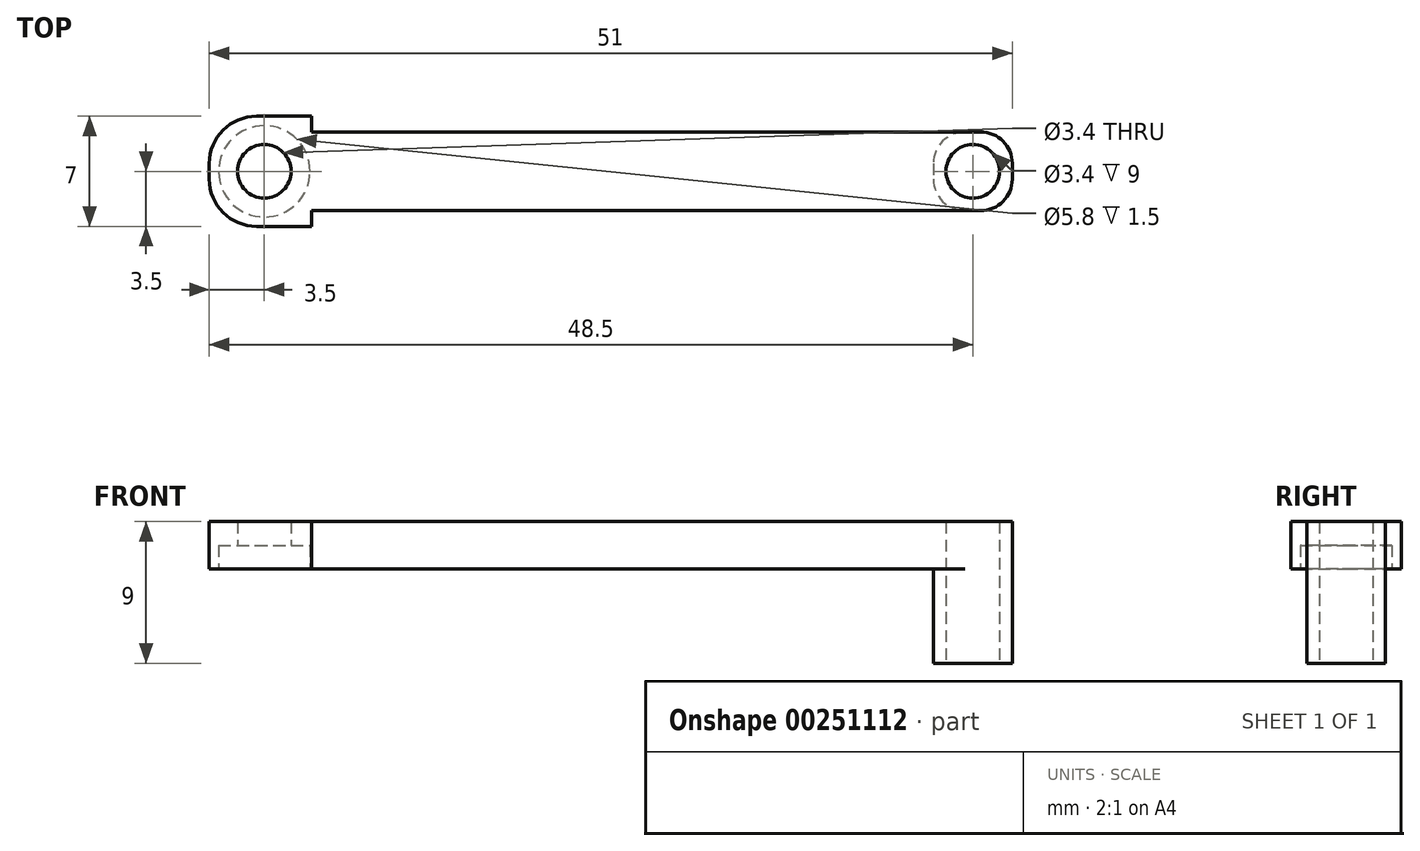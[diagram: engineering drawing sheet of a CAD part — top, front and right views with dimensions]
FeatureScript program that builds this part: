
annotation { "Feature Type Name" : "Feature", "Feature Type Description" : "" }
export const myFeature = defineFeature(function(context is Context, id is Id, definition is map)
    precondition{}
    {
        {
            var Q0;
            Q0=qCreatedBy(makeId("Top.planeOp"),FACE);
            var sketch = newSketch(context, id + "F0", { "sketchPlane" : qUnion([Q0])});
            skCircle(sketch, "E0", {"center": v(0, 0) * mm, "radius": 1.7 * mm});
            skCircle(sketch, "E1", {"center": v(45, 0) * mm, "radius": 1.7 * mm});
            skLineSegment(sketch, "E2", {"start": v(0, 0) * mm, "end": v(45, 0) * mm, "construction": true});
            skLineSegment(sketch, "E3", {"start": v(-2.5, 0) * mm, "end": v(-2.5, 2.5) * mm});
            skLineSegment(sketch, "E4", {"start": v(-2.5, 2.5) * mm, "end": v(47.5, 2.5) * mm});
            skLineSegment(sketch, "E5", {"start": v(47.5, 2.5) * mm, "end": v(47.5, 0) * mm});
            skLineSegment(sketch, "E6.MirrorCS", {"start": v(-2.5, 0) * mm, "end": v(-2.5, -2.5) * mm});
            skLineSegment(sketch, "E7.MirrorCS", {"start": v(-2.5, -2.5) * mm, "end": v(47.5, -2.5) * mm});
            skLineSegment(sketch, "E8.MirrorCS", {"start": v(47.5, -2.5) * mm, "end": v(47.5, 0) * mm});
            skSolve(sketch);
        }
        {
            var Q0;
            Q0=makeQuery(id+"F0.imprint","IMPRINT",FACE,{"disambiguationData":[TD([[makeQuery(id+"F0.imprint","IMPRINT",EDGE,{"derivedFrom":sQuery(id+"F0.wireOp",EDGE,"E0")}),-1.0]])]});
            extrude(context, id + "F1", {"entities" : qUnion([Q0]), "depth" : 3 * mm});
        }
        {
            var Q0;
            Q0=makeQuery(id+"F1.opExtrude","SWEPT_EDGE",EDGE,{"disambiguationData":[OSD([sQuery(id+"F0.wireOp",EDGE,"E3"),sQuery(id+"F0.wireOp",EDGE,"E4")])]});
            var Q1;
            Q1=makeQuery(id+"F1.opExtrude","SWEPT_EDGE",EDGE,{"disambiguationData":[OSD([sQuery(id+"F0.wireOp",EDGE,"E6.MirrorCS"),sQuery(id+"F0.wireOp",EDGE,"E7.MirrorCS")])]});
            var Q2;
            Q2=makeQuery(id+"F1.opExtrude","SWEPT_EDGE",EDGE,{"disambiguationData":[OSD([sQuery(id+"F0.wireOp",EDGE,"E4"),sQuery(id+"F0.wireOp",EDGE,"E5")])]});
            var Q3;
            Q3=makeQuery(id+"F1.opExtrude","SWEPT_EDGE",EDGE,{"disambiguationData":[OSD([sQuery(id+"F0.wireOp",EDGE,"E7.MirrorCS"),sQuery(id+"F0.wireOp",EDGE,"E8.MirrorCS")])]});
            fillet(context, id + "F2", {"entities" : qUnion([Q0, Q1, Q2, Q3]), "radius" : 2 * mm, "tangentPropagation" : true, "allowEdgeOverflow" : false});
        }
        {
            var Q0;
            Q0=makeQuery(id+"F1.opExtrude","CAP_FACE",FACE,{"disambiguationData":[OSD([sQuery(id+"F0.wireOp",EDGE,"E0"),sQuery(id+"F0.wireOp",EDGE,"E1"),sQuery(id+"F0.wireOp",EDGE,"E3"),sQuery(id+"F0.wireOp",EDGE,"E4"),sQuery(id+"F0.wireOp",EDGE,"E5"),sQuery(id+"F0.wireOp",EDGE,"E6.MirrorCS"),sQuery(id+"F0.wireOp",EDGE,"E7.MirrorCS"),sQuery(id+"F0.wireOp",EDGE,"E8.MirrorCS")])],"isStart":true});
            var sketch = newSketch(context, id + "F3", { "sketchPlane" : qUnion([Q0])});
            skArc(sketch, "E9.0", {"start": v(45.5, -2.5) * mm, "mid": v(46.91, -1.91) * mm, "end": v(47.5, -0.5) * mm});
            skPoint(sketch, "E10.0", {"position": v(47.5, 0) * mm});
            skPoint(sketch, "E11.0", {"position": v(46.91, 1.91) * mm});
            skArc(sketch, "E12.0", {"start": v(47.5, 0.5) * mm, "mid": v(46.91, 1.91) * mm, "end": v(45.5, 2.5) * mm});
            skLineSegment(sketch, "E13", {"start": v(45.5, -2.5) * mm, "end": v(42.5, -2.5) * mm});
            skLineSegment(sketch, "E14", {"start": v(42.5, -2.5) * mm, "end": v(42.5, 2.5) * mm});
            skLineSegment(sketch, "E15", {"start": v(42.5, 2.5) * mm, "end": v(45.5, 2.5) * mm});
            skCircle(sketch, "E16.0", {"center": v(45, 0) * mm, "radius": 1.7 * mm});
            skSolve(sketch);
        }
        {
            var Q0;
            Q0=makeQuery(id+"F3.imprint","IMPRINT",FACE,{"disambiguationData":[TD([[makeQuery(id+"F3.imprint","IMPRINT",EDGE,{"derivedFrom":sQuery(id+"F3.wireOp",EDGE,"E9.0")}),1.0]])]});
            extrude(context, id + "F4", {"entities" : qUnion([Q0]), "operationType" : NewBodyOperationType.ADD, "depth" : 6 * mm});
        }
        {
            var Q0;
            Q0=makeQuery(id+"F4.opExtrude","SWEPT_EDGE",EDGE,{"disambiguationData":[OSD([sQuery(id+"F0.wireOp",EDGE,"E4"),sQuery(id+"F3.wireOp",EDGE,"E13"),sQuery(id+"F3.wireOp",EDGE,"E14")])]});
            var Q1;
            Q1=makeQuery(id+"F4.opExtrude","SWEPT_EDGE",EDGE,{"disambiguationData":[OSD([sQuery(id+"F0.wireOp",EDGE,"E7.MirrorCS"),sQuery(id+"F3.wireOp",EDGE,"E14"),sQuery(id+"F3.wireOp",EDGE,"E15")])]});
            fillet(context, id + "F5", {"entities" : qUnion([Q0, Q1]), "radius" : 2 * mm, "tangentPropagation" : true, "allowEdgeOverflow" : false});
        }
        {
            var Q0;
            Q0=makeQuery(id+"F1.opExtrude","CAP_FACE",FACE,{"disambiguationData":[OSD([sQuery(id+"F0.wireOp",EDGE,"E0"),sQuery(id+"F0.wireOp",EDGE,"E1"),sQuery(id+"F0.wireOp",EDGE,"E3"),sQuery(id+"F0.wireOp",EDGE,"E4"),sQuery(id+"F0.wireOp",EDGE,"E5"),sQuery(id+"F0.wireOp",EDGE,"E6.MirrorCS"),sQuery(id+"F0.wireOp",EDGE,"E7.MirrorCS"),sQuery(id+"F0.wireOp",EDGE,"E8.MirrorCS")])],"isStart":false});
            var sketch = newSketch(context, id + "F6", { "sketchPlane" : qUnion([Q0])});
            skCircle(sketch, "E17.0", {"center": v(0, 0) * mm, "radius": 1.7 * mm});
            skArc(sketch, "E17.1", {"start": v(-0.5, 2.5) * mm, "mid": v(-1.91, 1.91) * mm, "end": v(-2.5, 0.5) * mm});
            skArc(sketch, "E17.2", {"start": v(-2.5, -0.5) * mm, "mid": v(-1.91, -1.91) * mm, "end": v(-0.5, -2.5) * mm});
            skCircle(sketch, "E17.4", {"center": v(0, 0) * mm, "radius": 1.7 * mm});
            skArc(sketch, "E17.5", {"start": v(-2.5, 0.5) * mm, "mid": v(-1.91, 1.91) * mm, "end": v(-0.5, 2.5) * mm});
            skArc(sketch, "E17.6", {"start": v(-0.5, -2.5) * mm, "mid": v(-1.91, -1.91) * mm, "end": v(-2.5, -0.5) * mm});
            skLineSegment(sketch, "E17.8", {"start": v(-2.5, -0.5) * mm, "end": v(-2.5, 0.5) * mm});
            skLineSegment(sketch, "E17.11", {"start": v(-2.5, -0.5) * mm, "end": v(-2.5, 0.5) * mm});
            skArc(sketch, "E18.0", {"start": v(-3.5, 0.5) * mm, "mid": v(-2.62, 2.62) * mm, "end": v(-0.5, 3.5) * mm});
            skLineSegment(sketch, "E18.1", {"start": v(-3.5, -0.5) * mm, "end": v(-3.5, 0.5) * mm});
            skArc(sketch, "E18.2", {"start": v(-0.5, -3.5) * mm, "mid": v(-2.62, -2.62) * mm, "end": v(-3.5, -0.5) * mm});
            skLineSegment(sketch, "E19", {"start": v(-0.5, 3.5) * mm, "end": v(3, 3.5) * mm});
            skLineSegment(sketch, "E20", {"start": v(3, 3.5) * mm, "end": v(3, 2.5) * mm});
            skLineSegment(sketch, "E21", {"start": v(3, 2.5) * mm, "end": v(3, -2.5) * mm});
            skLineSegment(sketch, "E22", {"start": v(-0.5, -3.5) * mm, "end": v(3, -3.5) * mm});
            skLineSegment(sketch, "E23", {"start": v(3, -3.5) * mm, "end": v(3, -2.5) * mm});
            skSolve(sketch);
        }
        {
            var Q0;
            Q0=qSketchRegion(id+"F6",true);
            var Q1;
            Q1=makeQuery(id+"F1.opExtrude","CAP_FACE",FACE,{"disambiguationData":[OSD([sQuery(id+"F0.wireOp",EDGE,"E0"),sQuery(id+"F0.wireOp",EDGE,"E1"),sQuery(id+"F0.wireOp",EDGE,"E3"),sQuery(id+"F0.wireOp",EDGE,"E4"),sQuery(id+"F0.wireOp",EDGE,"E5"),sQuery(id+"F0.wireOp",EDGE,"E6.MirrorCS"),sQuery(id+"F0.wireOp",EDGE,"E7.MirrorCS"),sQuery(id+"F0.wireOp",EDGE,"E8.MirrorCS")])],"isStart":true});
            extrude(context, id + "F7", {"entities" : qUnion([Q0]), "operationType" : NewBodyOperationType.ADD, "endBound" : BoundingType.UP_TO_SURFACE, "oppositeDirection" : true, "endBoundEntityFace" : qUnion([Q1]), "depth" : 25 * mm});
        }
        {
            var Q0;
            {var subQ0=sQuery(id+"F0.wireOp",EDGE,"E8.MirrorCS");var subQ1=sQuery(id+"F0.wireOp",EDGE,"E7.MirrorCS");var subQ2=sQuery(id+"F0.wireOp",EDGE,"E6.MirrorCS");var subQ3=sQuery(id+"F0.wireOp",EDGE,"E5");var subQ4=sQuery(id+"F0.wireOp",EDGE,"E4");var subQ5=sQuery(id+"F0.wireOp",EDGE,"E3");var subQ6=sQuery(id+"F0.wireOp",EDGE,"E1");var subQ7=sQuery(id+"F0.wireOp",EDGE,"E0");Q0=makeQuery(id+"F7.boolean.opBoolean","MERGE",FACE,{"derivedFrom":[makeQuery(id+"F1.opExtrude","CAP_FACE",FACE,{"disambiguationData":[OSD([subQ7,subQ6,subQ5,subQ4,subQ3,subQ2,subQ1,subQ0])],"isStart":true}),makeQuery(id+"F7.opExtrude","CAP_FACE",FACE,{"disambiguationData":[OSD([subQ7,subQ6,subQ5,subQ4,subQ3,subQ2,subQ1,subQ0])],"isStart":false})]});}
            var sketch = newSketch(context, id + "F8", { "sketchPlane" : qUnion([Q0])});
            skCircle(sketch, "E24.0", {"center": v(0, 0) * mm, "radius": 2.9 * mm});
            skSolve(sketch);
        }
        {
            var Q0;
            Q0=qSketchRegion(id+"F8",true);
            extrude(context, id + "F9", {"entities" : qUnion([Q0]), "operationType" : NewBodyOperationType.REMOVE, "oppositeDirection" : true, "depth" : 1.5 * mm});
        }
    });
